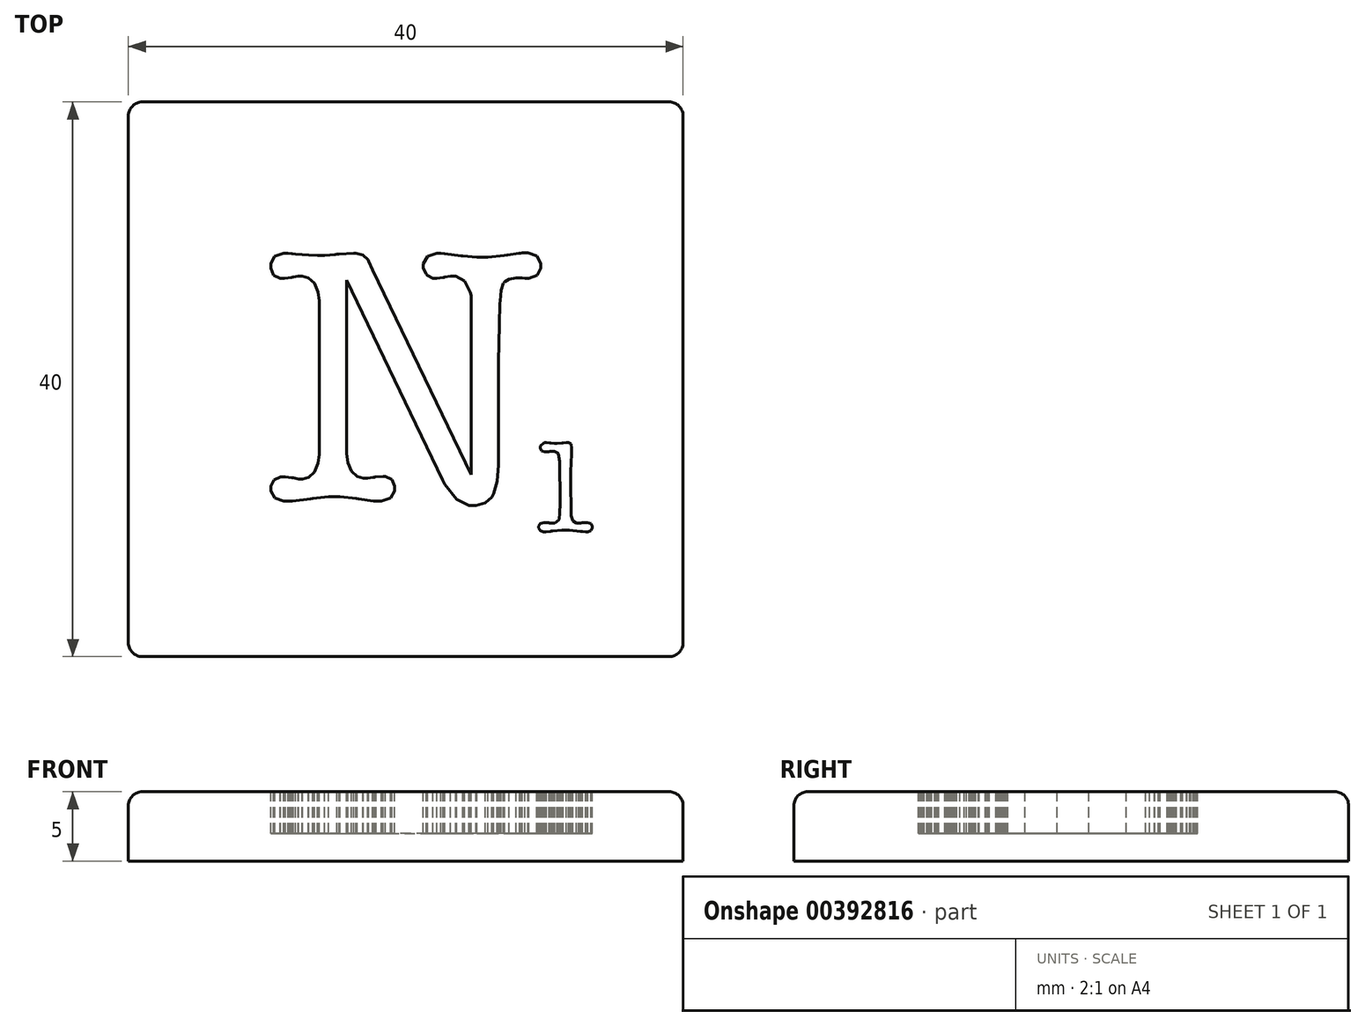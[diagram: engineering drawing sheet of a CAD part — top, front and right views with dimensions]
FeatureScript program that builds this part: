
annotation { "Feature Type Name" : "Feature", "Feature Type Description" : "" }
export const myFeature = defineFeature(function(context is Context, id is Id, definition is map)
    precondition{}
    {
        {
            var Q0;
            Q0=qCreatedBy(makeId("Top.planeOp"),FACE);
            var sketch = newSketch(context, id + "F0", { "sketchPlane" : qUnion([Q0])});
            skLineSegment(sketch, "E0.bottom", {"start": v(20, -20) * mm, "end": v(-20, -20) * mm});
            skLineSegment(sketch, "E0.top", {"start": v(20, 20) * mm, "end": v(-20, 20) * mm});
            skLineSegment(sketch, "E0.left", {"start": v(20, -20) * mm, "end": v(20, 20) * mm});
            skLineSegment(sketch, "E0.right", {"start": v(-20, -20) * mm, "end": v(-20, 20) * mm});
            skPoint(sketch, "E0.middle", {"position": v(0, 0) * mm});
            skSolve(sketch);
        }
        {
            var Q0;
            Q0=makeQuery(id+"F0.imprint","IMPRINT",FACE,{"disambiguationData":[TD([[makeQuery(id+"F0.imprint","IMPRINT",EDGE,{"derivedFrom":sQuery(id+"F0.wireOp",EDGE,"E0.bottom")}),-1.0]])]});
            extrude(context, id + "F1", {"entities" : qUnion([Q0]), "depth" : -5 * mm});
        }
        {
            var Q0;
            Q0=makeQuery(id+"F1.opExtrude","CAP_FACE",FACE,{"disambiguationData":[OSD([sQuery(id+"F0.wireOp",EDGE,"E0.bottom"),sQuery(id+"F0.wireOp",EDGE,"E0.top"),sQuery(id+"F0.wireOp",EDGE,"E0.left"),sQuery(id+"F0.wireOp",EDGE,"E0.right")])],"isStart":true});
            var Q1;
            Q1=makeQuery(id+"F1.opExtrude","SWEPT_EDGE",EDGE,{"disambiguationData":[OSD([sQuery(id+"F0.wireOp",EDGE,"E0.top"),sQuery(id+"F0.wireOp",EDGE,"E0.right")])]});
            var Q2;
            Q2=makeQuery(id+"F1.opExtrude","SWEPT_EDGE",EDGE,{"disambiguationData":[OSD([sQuery(id+"F0.wireOp",EDGE,"E0.top"),sQuery(id+"F0.wireOp",EDGE,"E0.left")])]});
            var Q3;
            Q3=makeQuery(id+"F1.opExtrude","SWEPT_EDGE",EDGE,{"disambiguationData":[OSD([sQuery(id+"F0.wireOp",EDGE,"E0.bottom"),sQuery(id+"F0.wireOp",EDGE,"E0.right")])]});
            var Q4;
            Q4=makeQuery(id+"F1.opExtrude","SWEPT_EDGE",EDGE,{"disambiguationData":[OSD([sQuery(id+"F0.wireOp",EDGE,"E0.bottom"),sQuery(id+"F0.wireOp",EDGE,"E0.left")])]});
            fillet(context, id + "F2", {"entities" : qUnion([Q0, Q1, Q2, Q3, Q4]), "radius" : 1 * mm, "tangentPropagation" : true, "allowEdgeOverflow" : false});
        }
        {
            var Q0;
            Q0=qCreatedBy(makeId("Top.planeOp"),FACE);
            var sketch = newSketch(context, id + "F3", { "sketchPlane" : qUnion([Q0])});
            skLineSegment(sketch, "E1", {"start": v(-2.38, 7.9) * mm, "end": v(4.74, -6.9) * mm});
            skLineSegment(sketch, "E2", {"start": v(4.74, -6.9) * mm, "end": v(4.74, 3.77) * mm});
            skLineSegment(sketch, "E3", {"start": v(4.74, 3.77) * mm, "end": v(4.74, 4.17) * mm});
            skLineSegment(sketch, "E4", {"start": v(4.74, 4.17) * mm, "end": v(4.73, 5.37) * mm});
            skLineSegment(sketch, "E5", {"start": v(4.73, 5.37) * mm, "end": v(4.71, 6.01) * mm});
            skLineSegment(sketch, "E6", {"start": v(4.71, 6.01) * mm, "end": v(4.7, 6.05) * mm});
            skLineSegment(sketch, "E7", {"start": v(4.7, 6.05) * mm, "end": v(4.67, 6.28) * mm});
            skLineSegment(sketch, "E8", {"start": v(4.67, 6.28) * mm, "end": v(4.26, 7.08) * mm});
            skLineSegment(sketch, "E9", {"start": v(4.26, 7.08) * mm, "end": v(3.6, 7.42) * mm});
            skLineSegment(sketch, "E10", {"start": v(3.6, 7.42) * mm, "end": v(3.39, 7.42) * mm});
            skLineSegment(sketch, "E11", {"start": v(3.39, 7.42) * mm, "end": v(3.23, 7.42) * mm});
            skLineSegment(sketch, "E12", {"start": v(3.23, 7.42) * mm, "end": v(2.82, 7.37) * mm});
            skLineSegment(sketch, "E13", {"start": v(2.82, 7.37) * mm, "end": v(2.75, 7.36) * mm});
            skLineSegment(sketch, "E14", {"start": v(2.75, 7.36) * mm, "end": v(2.68, 7.34) * mm});
            skLineSegment(sketch, "E15", {"start": v(2.68, 7.34) * mm, "end": v(2.26, 7.29) * mm});
            skLineSegment(sketch, "E16", {"start": v(2.26, 7.29) * mm, "end": v(2.12, 7.29) * mm});
            skLineSegment(sketch, "E17", {"start": v(2.12, 7.29) * mm, "end": v(1.97, 7.29) * mm});
            skLineSegment(sketch, "E18", {"start": v(1.97, 7.29) * mm, "end": v(1.56, 7.5) * mm});
            skLineSegment(sketch, "E19", {"start": v(1.56, 7.5) * mm, "end": v(1.52, 7.54) * mm});
            skLineSegment(sketch, "E20", {"start": v(1.52, 7.54) * mm, "end": v(1.48, 7.58) * mm});
            skLineSegment(sketch, "E21", {"start": v(1.48, 7.58) * mm, "end": v(1.27, 8) * mm});
            skLineSegment(sketch, "E22", {"start": v(1.27, 8) * mm, "end": v(1.27, 8.14) * mm});
            skLineSegment(sketch, "E23", {"start": v(1.27, 8.14) * mm, "end": v(1.27, 8.32) * mm});
            skLineSegment(sketch, "E24", {"start": v(1.27, 8.32) * mm, "end": v(1.57, 8.85) * mm});
            skLineSegment(sketch, "E25", {"start": v(1.57, 8.85) * mm, "end": v(2.24, 9.09) * mm});
            skLineSegment(sketch, "E26", {"start": v(2.24, 9.09) * mm, "end": v(2.46, 9.09) * mm});
            skLineSegment(sketch, "E27", {"start": v(2.46, 9.09) * mm, "end": v(2.55, 9.09) * mm});
            skLineSegment(sketch, "E28", {"start": v(2.55, 9.09) * mm, "end": v(2.79, 9.07) * mm});
            skLineSegment(sketch, "E29", {"start": v(2.79, 9.07) * mm, "end": v(2.8, 9.06) * mm});
            skLineSegment(sketch, "E30", {"start": v(2.8, 9.06) * mm, "end": v(4, 8.9) * mm});
            skLineSegment(sketch, "E31", {"start": v(4, 8.9) * mm, "end": v(4.13, 8.89) * mm});
            skLineSegment(sketch, "E32", {"start": v(4.13, 8.89) * mm, "end": v(5.14, 8.8) * mm});
            skLineSegment(sketch, "E33", {"start": v(5.14, 8.8) * mm, "end": v(5.48, 8.8) * mm});
            skLineSegment(sketch, "E34", {"start": v(5.48, 8.8) * mm, "end": v(5.93, 8.8) * mm});
            skLineSegment(sketch, "E35", {"start": v(5.93, 8.8) * mm, "end": v(7.11, 8.93) * mm});
            skLineSegment(sketch, "E36", {"start": v(7.11, 8.93) * mm, "end": v(7.3, 8.96) * mm});
            skLineSegment(sketch, "E37", {"start": v(7.3, 8.96) * mm, "end": v(7.37, 8.97) * mm});
            skLineSegment(sketch, "E38", {"start": v(7.37, 8.97) * mm, "end": v(8.14, 9.08) * mm});
            skLineSegment(sketch, "E39", {"start": v(8.14, 9.08) * mm, "end": v(8.23, 9.09) * mm});
            skLineSegment(sketch, "E40", {"start": v(8.23, 9.09) * mm, "end": v(8.27, 9.09) * mm});
            skLineSegment(sketch, "E41", {"start": v(8.27, 9.09) * mm, "end": v(8.4, 9.11) * mm});
            skLineSegment(sketch, "E42", {"start": v(8.4, 9.11) * mm, "end": v(8.41, 9.11) * mm});
            skLineSegment(sketch, "E43", {"start": v(8.41, 9.11) * mm, "end": v(8.6, 9.11) * mm});
            skLineSegment(sketch, "E44", {"start": v(8.6, 9.11) * mm, "end": v(8.81, 9.11) * mm});
            skLineSegment(sketch, "E45", {"start": v(8.81, 9.11) * mm, "end": v(9.45, 8.88) * mm});
            skLineSegment(sketch, "E46", {"start": v(9.45, 8.88) * mm, "end": v(9.74, 8.36) * mm});
            skLineSegment(sketch, "E47", {"start": v(9.74, 8.36) * mm, "end": v(9.74, 8.19) * mm});
            skLineSegment(sketch, "E48", {"start": v(9.74, 8.19) * mm, "end": v(9.74, 8.02) * mm});
            skLineSegment(sketch, "E49", {"start": v(9.74, 8.02) * mm, "end": v(9.47, 7.51) * mm});
            skLineSegment(sketch, "E50", {"start": v(9.47, 7.51) * mm, "end": v(8.88, 7.29) * mm});
            skLineSegment(sketch, "E51", {"start": v(8.88, 7.29) * mm, "end": v(8.68, 7.29) * mm});
            skLineSegment(sketch, "E52", {"start": v(8.68, 7.29) * mm, "end": v(8.6, 7.29) * mm});
            skLineSegment(sketch, "E53", {"start": v(8.6, 7.29) * mm, "end": v(8.4, 7.31) * mm});
            skLineSegment(sketch, "E54", {"start": v(8.4, 7.31) * mm, "end": v(8.39, 7.32) * mm});
            skLineSegment(sketch, "E55", {"start": v(8.39, 7.32) * mm, "end": v(8.12, 7.32) * mm});
            skLineSegment(sketch, "E56", {"start": v(8.12, 7.32) * mm, "end": v(7.96, 7.32) * mm});
            skLineSegment(sketch, "E57", {"start": v(7.96, 7.32) * mm, "end": v(7.47, 7.23) * mm});
            skLineSegment(sketch, "E58", {"start": v(7.47, 7.23) * mm, "end": v(7.13, 7.03) * mm});
            skLineSegment(sketch, "E59", {"start": v(7.13, 7.03) * mm, "end": v(7.1, 6.97) * mm});
            skLineSegment(sketch, "E60", {"start": v(7.1, 6.97) * mm, "end": v(7.05, 6.92) * mm});
            skLineSegment(sketch, "E61", {"start": v(7.05, 6.92) * mm, "end": v(6.9, 6.42) * mm});
            skLineSegment(sketch, "E62", {"start": v(6.9, 6.42) * mm, "end": v(6.8, 5.66) * mm});
            skLineSegment(sketch, "E63", {"start": v(6.8, 5.66) * mm, "end": v(6.8, 5.46) * mm});
            skLineSegment(sketch, "E64", {"start": v(6.8, 5.46) * mm, "end": v(6.75, 3.95) * mm});
            skLineSegment(sketch, "E65", {"start": v(6.75, 3.95) * mm, "end": v(6.7, 1.26) * mm});
            skLineSegment(sketch, "E66", {"start": v(6.7, 1.26) * mm, "end": v(6.7, -5.8) * mm});
            skLineSegment(sketch, "E67", {"start": v(6.7, -5.8) * mm, "end": v(6.7, -6.2) * mm});
            skLineSegment(sketch, "E68", {"start": v(6.7, -6.2) * mm, "end": v(6.6, -7.36) * mm});
            skLineSegment(sketch, "E69", {"start": v(6.6, -7.36) * mm, "end": v(6.35, -8.25) * mm});
            skLineSegment(sketch, "E70", {"start": v(6.35, -8.25) * mm, "end": v(6.28, -8.37) * mm});
            skLineSegment(sketch, "E71", {"start": v(6.28, -8.37) * mm, "end": v(6.21, -8.5) * mm});
            skLineSegment(sketch, "E72", {"start": v(6.21, -8.5) * mm, "end": v(5.72, -8.93) * mm});
            skLineSegment(sketch, "E73", {"start": v(5.72, -8.93) * mm, "end": v(5.08, -9.11) * mm});
            skLineSegment(sketch, "E74", {"start": v(5.08, -9.11) * mm, "end": v(4.87, -9.11) * mm});
            skLineSegment(sketch, "E75", {"start": v(4.87, -9.11) * mm, "end": v(4.57, -9.11) * mm});
            skLineSegment(sketch, "E76", {"start": v(4.57, -9.11) * mm, "end": v(3.67, -8.65) * mm});
            skLineSegment(sketch, "E77", {"start": v(3.67, -8.65) * mm, "end": v(2.82, -7.57) * mm});
            skLineSegment(sketch, "E78", {"start": v(2.82, -7.57) * mm, "end": v(2.67, -7.26) * mm});
            skLineSegment(sketch, "E79", {"start": v(2.67, -7.26) * mm, "end": v(-4.26, 7.16) * mm});
            skLineSegment(sketch, "E80", {"start": v(-4.26, 7.16) * mm, "end": v(-4.26, -5.15) * mm});
            skLineSegment(sketch, "E81", {"start": v(-4.26, -5.15) * mm, "end": v(-4.26, -5.36) * mm});
            skLineSegment(sketch, "E82", {"start": v(-4.26, -5.36) * mm, "end": v(-4.18, -6.01) * mm});
            skLineSegment(sketch, "E83", {"start": v(-4.18, -6.01) * mm, "end": v(-3.92, -6.63) * mm});
            skLineSegment(sketch, "E84", {"start": v(-3.92, -6.63) * mm, "end": v(-3.5, -7) * mm});
            skLineSegment(sketch, "E85", {"start": v(-3.5, -7) * mm, "end": v(-3.06, -7.13) * mm});
            skLineSegment(sketch, "E86", {"start": v(-3.06, -7.13) * mm, "end": v(-2.91, -7.13) * mm});
            skLineSegment(sketch, "E87", {"start": v(-2.91, -7.13) * mm, "end": v(-2.75, -7.13) * mm});
            skLineSegment(sketch, "E88", {"start": v(-2.75, -7.13) * mm, "end": v(-2.35, -7.07) * mm});
            skLineSegment(sketch, "E89", {"start": v(-2.35, -7.07) * mm, "end": v(-2.28, -7.06) * mm});
            skLineSegment(sketch, "E90", {"start": v(-2.28, -7.06) * mm, "end": v(-2.2, -7.05) * mm});
            skLineSegment(sketch, "E91", {"start": v(-2.2, -7.05) * mm, "end": v(-1.64, -7) * mm});
            skLineSegment(sketch, "E92", {"start": v(-1.64, -7) * mm, "end": v(-1.48, -7) * mm});
            skLineSegment(sketch, "E93", {"start": v(-1.48, -7) * mm, "end": v(-1, -7.22) * mm});
            skLineSegment(sketch, "E94", {"start": v(-1, -7.22) * mm, "end": v(-0.8, -7.7) * mm});
            skLineSegment(sketch, "E95", {"start": v(-0.8, -7.7) * mm, "end": v(-0.8, -7.87) * mm});
            skLineSegment(sketch, "E96", {"start": v(-0.8, -7.87) * mm, "end": v(-0.8, -8.04) * mm});
            skLineSegment(sketch, "E97", {"start": v(-0.8, -8.04) * mm, "end": v(-1.1, -8.57) * mm});
            skLineSegment(sketch, "E98", {"start": v(-1.1, -8.57) * mm, "end": v(-1.76, -8.8) * mm});
            skLineSegment(sketch, "E99", {"start": v(-1.76, -8.8) * mm, "end": v(-1.99, -8.8) * mm});
            skLineSegment(sketch, "E100", {"start": v(-1.99, -8.8) * mm, "end": v(-2.14, -8.8) * mm});
            skLineSegment(sketch, "E101", {"start": v(-2.14, -8.8) * mm, "end": v(-2.17, -8.8) * mm});
            skLineSegment(sketch, "E102", {"start": v(-2.17, -8.8) * mm, "end": v(-2.29, -8.77) * mm});
            skLineSegment(sketch, "E103", {"start": v(-2.29, -8.77) * mm, "end": v(-2.33, -8.77) * mm});
            skLineSegment(sketch, "E104", {"start": v(-2.33, -8.77) * mm, "end": v(-3.41, -8.61) * mm});
            skLineSegment(sketch, "E105", {"start": v(-3.41, -8.61) * mm, "end": v(-3.56, -8.6) * mm});
            skLineSegment(sketch, "E106", {"start": v(-3.56, -8.6) * mm, "end": v(-4.72, -8.48) * mm});
            skLineSegment(sketch, "E107", {"start": v(-4.72, -8.48) * mm, "end": v(-5.1, -8.48) * mm});
            skLineSegment(sketch, "E108", {"start": v(-5.1, -8.48) * mm, "end": v(-5.55, -8.48) * mm});
            skLineSegment(sketch, "E109", {"start": v(-5.55, -8.48) * mm, "end": v(-6.7, -8.6) * mm});
            skLineSegment(sketch, "E110", {"start": v(-6.7, -8.6) * mm, "end": v(-6.88, -8.61) * mm});
            skLineSegment(sketch, "E111", {"start": v(-6.88, -8.61) * mm, "end": v(-8.18, -8.77) * mm});
            skLineSegment(sketch, "E112", {"start": v(-8.18, -8.77) * mm, "end": v(-8.22, -8.77) * mm});
            skLineSegment(sketch, "E113", {"start": v(-8.22, -8.77) * mm, "end": v(-8.34, -8.8) * mm});
            skLineSegment(sketch, "E114", {"start": v(-8.34, -8.8) * mm, "end": v(-8.36, -8.8) * mm});
            skLineSegment(sketch, "E115", {"start": v(-8.36, -8.8) * mm, "end": v(-8.57, -8.8) * mm});
            skLineSegment(sketch, "E116", {"start": v(-8.57, -8.8) * mm, "end": v(-8.79, -8.8) * mm});
            skLineSegment(sketch, "E117", {"start": v(-8.79, -8.8) * mm, "end": v(-9.43, -8.57) * mm});
            skLineSegment(sketch, "E118", {"start": v(-9.43, -8.57) * mm, "end": v(-9.71, -8.04) * mm});
            skLineSegment(sketch, "E119", {"start": v(-9.71, -8.04) * mm, "end": v(-9.71, -7.87) * mm});
            skLineSegment(sketch, "E120", {"start": v(-9.71, -7.87) * mm, "end": v(-9.71, -7.72) * mm});
            skLineSegment(sketch, "E121", {"start": v(-9.71, -7.72) * mm, "end": v(-9.5, -7.26) * mm});
            skLineSegment(sketch, "E122", {"start": v(-9.5, -7.26) * mm, "end": v(-9.02, -7.05) * mm});
            skLineSegment(sketch, "E123", {"start": v(-9.02, -7.05) * mm, "end": v(-8.86, -7.05) * mm});
            skLineSegment(sketch, "E124", {"start": v(-8.86, -7.05) * mm, "end": v(-8.69, -7.05) * mm});
            skLineSegment(sketch, "E125", {"start": v(-8.69, -7.05) * mm, "end": v(-8.25, -7.1) * mm});
            skLineSegment(sketch, "E126", {"start": v(-8.25, -7.1) * mm, "end": v(-8.15, -7.1) * mm});
            skLineSegment(sketch, "E127", {"start": v(-8.15, -7.1) * mm, "end": v(-8.1, -7.12) * mm});
            skLineSegment(sketch, "E128", {"start": v(-8.1, -7.12) * mm, "end": v(-7.72, -7.18) * mm});
            skLineSegment(sketch, "E129", {"start": v(-7.72, -7.18) * mm, "end": v(-7.6, -7.18) * mm});
            skLineSegment(sketch, "E130", {"start": v(-7.6, -7.18) * mm, "end": v(-7.45, -7.18) * mm});
            skLineSegment(sketch, "E131", {"start": v(-7.45, -7.18) * mm, "end": v(-7, -7.06) * mm});
            skLineSegment(sketch, "E132", {"start": v(-7, -7.06) * mm, "end": v(-6.58, -6.69) * mm});
            skLineSegment(sketch, "E133", {"start": v(-6.58, -6.69) * mm, "end": v(-6.33, -6.07) * mm});
            skLineSegment(sketch, "E134", {"start": v(-6.33, -6.07) * mm, "end": v(-6.24, -5.42) * mm});
            skLineSegment(sketch, "E135", {"start": v(-6.24, -5.42) * mm, "end": v(-6.24, -5.2) * mm});
            skLineSegment(sketch, "E136", {"start": v(-6.24, -5.2) * mm, "end": v(-6.24, -3.35) * mm});
            skLineSegment(sketch, "E137", {"start": v(-6.24, -3.35) * mm, "end": v(-6.22, -1.02) * mm});
            skLineSegment(sketch, "E138", {"start": v(-6.22, -1.02) * mm, "end": v(-6.22, 1.26) * mm});
            skLineSegment(sketch, "E139", {"start": v(-6.22, 1.26) * mm, "end": v(-6.24, 5.44) * mm});
            skLineSegment(sketch, "E140", {"start": v(-6.24, 5.44) * mm, "end": v(-6.24, 5.66) * mm});
            skLineSegment(sketch, "E141", {"start": v(-6.24, 5.66) * mm, "end": v(-6.33, 6.3) * mm});
            skLineSegment(sketch, "E142", {"start": v(-6.33, 6.3) * mm, "end": v(-6.59, 6.93) * mm});
            skLineSegment(sketch, "E143", {"start": v(-6.59, 6.93) * mm, "end": v(-7.02, 7.3) * mm});
            skLineSegment(sketch, "E144", {"start": v(-7.02, 7.3) * mm, "end": v(-7.47, 7.42) * mm});
            skLineSegment(sketch, "E145", {"start": v(-7.47, 7.42) * mm, "end": v(-7.62, 7.42) * mm});
            skLineSegment(sketch, "E146", {"start": v(-7.62, 7.42) * mm, "end": v(-7.75, 7.42) * mm});
            skLineSegment(sketch, "E147", {"start": v(-7.75, 7.42) * mm, "end": v(-8.1, 7.38) * mm});
            skLineSegment(sketch, "E148", {"start": v(-8.1, 7.38) * mm, "end": v(-8.15, 7.37) * mm});
            skLineSegment(sketch, "E149", {"start": v(-8.15, 7.37) * mm, "end": v(-8.23, 7.36) * mm});
            skLineSegment(sketch, "E150", {"start": v(-8.23, 7.36) * mm, "end": v(-8.73, 7.29) * mm});
            skLineSegment(sketch, "E151", {"start": v(-8.73, 7.29) * mm, "end": v(-8.9, 7.29) * mm});
            skLineSegment(sketch, "E152", {"start": v(-8.9, 7.29) * mm, "end": v(-9.05, 7.29) * mm});
            skLineSegment(sketch, "E153", {"start": v(-9.05, 7.29) * mm, "end": v(-9.53, 7.5) * mm});
            skLineSegment(sketch, "E154", {"start": v(-9.53, 7.5) * mm, "end": v(-9.74, 8) * mm});
            skLineSegment(sketch, "E155", {"start": v(-9.74, 8) * mm, "end": v(-9.74, 8.16) * mm});
            skLineSegment(sketch, "E156", {"start": v(-9.74, 8.16) * mm, "end": v(-9.74, 8.34) * mm});
            skLineSegment(sketch, "E157", {"start": v(-9.74, 8.34) * mm, "end": v(-9.45, 8.86) * mm});
            skLineSegment(sketch, "E158", {"start": v(-9.45, 8.86) * mm, "end": v(-8.81, 9.09) * mm});
            skLineSegment(sketch, "E159", {"start": v(-8.81, 9.09) * mm, "end": v(-8.6, 9.09) * mm});
            skLineSegment(sketch, "E160", {"start": v(-8.6, 9.09) * mm, "end": v(-8.5, 9.09) * mm});
            skLineSegment(sketch, "E161", {"start": v(-8.5, 9.09) * mm, "end": v(-8.22, 9.07) * mm});
            skLineSegment(sketch, "E162", {"start": v(-8.22, 9.07) * mm, "end": v(-8.18, 9.06) * mm});
            skLineSegment(sketch, "E163", {"start": v(-8.18, 9.06) * mm, "end": v(-7.96, 9.04) * mm});
            skLineSegment(sketch, "E164", {"start": v(-7.96, 9.04) * mm, "end": v(-7, 8.96) * mm});
            skLineSegment(sketch, "E165", {"start": v(-7, 8.96) * mm, "end": v(-6.36, 8.93) * mm});
            skLineSegment(sketch, "E166", {"start": v(-6.36, 8.93) * mm, "end": v(-6.14, 8.93) * mm});
            skLineSegment(sketch, "E167", {"start": v(-6.14, 8.93) * mm, "end": v(-5.84, 8.93) * mm});
            skLineSegment(sketch, "E168", {"start": v(-5.84, 8.93) * mm, "end": v(-5.08, 9) * mm});
            skLineSegment(sketch, "E169", {"start": v(-5.08, 9) * mm, "end": v(-4.95, 9) * mm});
            skLineSegment(sketch, "E170", {"start": v(-4.95, 9) * mm, "end": v(-4.82, 9.02) * mm});
            skLineSegment(sketch, "E171", {"start": v(-4.82, 9.02) * mm, "end": v(-3.76, 9.09) * mm});
            skLineSegment(sketch, "E172", {"start": v(-3.76, 9.09) * mm, "end": v(-3.59, 9.09) * mm});
            skLineSegment(sketch, "E173", {"start": v(-3.59, 9.09) * mm, "end": v(-3.08, 8.95) * mm});
            skLineSegment(sketch, "E174", {"start": v(-3.08, 8.95) * mm, "end": v(-2.72, 8.63) * mm});
            skLineSegment(sketch, "E175", {"start": v(-2.72, 8.63) * mm, "end": v(-2.67, 8.53) * mm});
            skLineSegment(sketch, "E176", {"start": v(-2.67, 8.53) * mm, "end": v(-2.38, 7.9) * mm});
            skSolve(sketch);
        }
        {
            var Q0;
            Q0=qCreatedBy(makeId("Top.planeOp"),FACE);
            var sketch = newSketch(context, id + "F4", { "sketchPlane" : qUnion([Q0])});
            skLineSegment(sketch, "E177", {"start": v(11.13, -8.76) * mm, "end": v(11.1, -6) * mm});
            skLineSegment(sketch, "E178", {"start": v(11.1, -6) * mm, "end": v(11.1, -5.92) * mm});
            skLineSegment(sketch, "E179", {"start": v(11.1, -5.92) * mm, "end": v(11.02, -5.38) * mm});
            skLineSegment(sketch, "E180", {"start": v(11.02, -5.38) * mm, "end": v(11, -5.35) * mm});
            skLineSegment(sketch, "E181", {"start": v(11, -5.35) * mm, "end": v(10.99, -5.32) * mm});
            skLineSegment(sketch, "E182", {"start": v(10.99, -5.32) * mm, "end": v(10.73, -5.19) * mm});
            skLineSegment(sketch, "E183", {"start": v(10.73, -5.19) * mm, "end": v(10.64, -5.19) * mm});
            skLineSegment(sketch, "E184", {"start": v(10.64, -5.19) * mm, "end": v(10.57, -5.19) * mm});
            skLineSegment(sketch, "E185", {"start": v(10.57, -5.19) * mm, "end": v(10.4, -5.2) * mm});
            skLineSegment(sketch, "E186", {"start": v(10.4, -5.2) * mm, "end": v(10.37, -5.21) * mm});
            skLineSegment(sketch, "E187", {"start": v(10.37, -5.21) * mm, "end": v(10.34, -5.22) * mm});
            skLineSegment(sketch, "E188", {"start": v(10.34, -5.22) * mm, "end": v(10.15, -5.24) * mm});
            skLineSegment(sketch, "E189", {"start": v(10.15, -5.24) * mm, "end": v(10.1, -5.24) * mm});
            skLineSegment(sketch, "E190", {"start": v(10.1, -5.24) * mm, "end": v(10.02, -5.24) * mm});
            skLineSegment(sketch, "E191", {"start": v(10.02, -5.24) * mm, "end": v(9.81, -5.15) * mm});
            skLineSegment(sketch, "E192", {"start": v(9.81, -5.15) * mm, "end": v(9.72, -4.97) * mm});
            skLineSegment(sketch, "E193", {"start": v(9.72, -4.97) * mm, "end": v(9.72, -4.9) * mm});
            skLineSegment(sketch, "E194", {"start": v(9.72, -4.9) * mm, "end": v(9.72, -4.82) * mm});
            skLineSegment(sketch, "E195", {"start": v(9.72, -4.82) * mm, "end": v(9.98, -4.57) * mm});
            skLineSegment(sketch, "E196", {"start": v(9.98, -4.57) * mm, "end": v(10.07, -4.57) * mm});
            skLineSegment(sketch, "E197", {"start": v(10.07, -4.57) * mm, "end": v(10.16, -4.57) * mm});
            skLineSegment(sketch, "E198", {"start": v(10.16, -4.57) * mm, "end": v(10.39, -4.59) * mm});
            skLineSegment(sketch, "E199", {"start": v(10.39, -4.59) * mm, "end": v(10.43, -4.6) * mm});
            skLineSegment(sketch, "E200", {"start": v(10.43, -4.6) * mm, "end": v(10.47, -4.6) * mm});
            skLineSegment(sketch, "E201", {"start": v(10.47, -4.6) * mm, "end": v(10.72, -4.62) * mm});
            skLineSegment(sketch, "E202", {"start": v(10.72, -4.62) * mm, "end": v(10.8, -4.62) * mm});
            skLineSegment(sketch, "E203", {"start": v(10.8, -4.62) * mm, "end": v(10.93, -4.62) * mm});
            skLineSegment(sketch, "E204", {"start": v(10.93, -4.62) * mm, "end": v(11.28, -4.6) * mm});
            skLineSegment(sketch, "E205", {"start": v(11.28, -4.6) * mm, "end": v(11.3, -4.6) * mm});
            skLineSegment(sketch, "E206", {"start": v(11.3, -4.6) * mm, "end": v(11.36, -4.6) * mm});
            skLineSegment(sketch, "E207", {"start": v(11.36, -4.6) * mm, "end": v(11.6, -4.57) * mm});
            skLineSegment(sketch, "E208", {"start": v(11.6, -4.57) * mm, "end": v(11.67, -4.57) * mm});
            skLineSegment(sketch, "E209", {"start": v(11.67, -4.57) * mm, "end": v(11.74, -4.57) * mm});
            skLineSegment(sketch, "E210", {"start": v(11.74, -4.57) * mm, "end": v(11.92, -4.67) * mm});
            skLineSegment(sketch, "E211", {"start": v(11.92, -4.67) * mm, "end": v(11.93, -4.7) * mm});
            skLineSegment(sketch, "E212", {"start": v(11.93, -4.7) * mm, "end": v(11.93, -4.7) * mm});
            skLineSegment(sketch, "E213", {"start": v(11.93, -4.7) * mm, "end": v(11.97, -4.92) * mm});
            skLineSegment(sketch, "E214", {"start": v(11.97, -4.92) * mm, "end": v(11.97, -4.99) * mm});
            skLineSegment(sketch, "E215", {"start": v(11.97, -4.99) * mm, "end": v(11.97, -5.05) * mm});
            skLineSegment(sketch, "E216", {"start": v(11.97, -5.05) * mm, "end": v(11.96, -5.18) * mm});
            skLineSegment(sketch, "E217", {"start": v(11.96, -5.18) * mm, "end": v(11.96, -5.22) * mm});
            skLineSegment(sketch, "E218", {"start": v(11.96, -5.22) * mm, "end": v(11.95, -5.39) * mm});
            skLineSegment(sketch, "E219", {"start": v(11.95, -5.39) * mm, "end": v(11.91, -6.65) * mm});
            skLineSegment(sketch, "E220", {"start": v(11.91, -6.65) * mm, "end": v(11.91, -7.07) * mm});
            skLineSegment(sketch, "E221", {"start": v(11.91, -7.07) * mm, "end": v(11.91, -8.14) * mm});
            skLineSegment(sketch, "E222", {"start": v(11.91, -8.14) * mm, "end": v(11.92, -8.85) * mm});
            skLineSegment(sketch, "E223", {"start": v(11.92, -8.85) * mm, "end": v(11.92, -8.93) * mm});
            skLineSegment(sketch, "E224", {"start": v(11.92, -8.93) * mm, "end": v(11.92, -9.03) * mm});
            skLineSegment(sketch, "E225", {"start": v(11.92, -9.03) * mm, "end": v(11.94, -9.55) * mm});
            skLineSegment(sketch, "E226", {"start": v(11.94, -9.55) * mm, "end": v(11.94, -9.72) * mm});
            skLineSegment(sketch, "E227", {"start": v(11.94, -9.72) * mm, "end": v(11.94, -9.83) * mm});
            skLineSegment(sketch, "E228", {"start": v(11.94, -9.83) * mm, "end": v(12.05, -10.21) * mm});
            skLineSegment(sketch, "E229", {"start": v(12.05, -10.21) * mm, "end": v(12.3, -10.38) * mm});
            skLineSegment(sketch, "E230", {"start": v(12.3, -10.38) * mm, "end": v(12.38, -10.38) * mm});
            skLineSegment(sketch, "E231", {"start": v(12.38, -10.38) * mm, "end": v(12.46, -10.38) * mm});
            skLineSegment(sketch, "E232", {"start": v(12.46, -10.38) * mm, "end": v(12.66, -10.36) * mm});
            skLineSegment(sketch, "E233", {"start": v(12.66, -10.36) * mm, "end": v(12.7, -10.36) * mm});
            skLineSegment(sketch, "E234", {"start": v(12.7, -10.36) * mm, "end": v(12.73, -10.35) * mm});
            skLineSegment(sketch, "E235", {"start": v(12.73, -10.35) * mm, "end": v(13, -10.33) * mm});
            skLineSegment(sketch, "E236", {"start": v(13, -10.33) * mm, "end": v(13.1, -10.33) * mm});
            skLineSegment(sketch, "E237", {"start": v(13.1, -10.33) * mm, "end": v(13.35, -10.42) * mm});
            skLineSegment(sketch, "E238", {"start": v(13.35, -10.42) * mm, "end": v(13.46, -10.6) * mm});
            skLineSegment(sketch, "E239", {"start": v(13.46, -10.6) * mm, "end": v(13.46, -10.67) * mm});
            skLineSegment(sketch, "E240", {"start": v(13.46, -10.67) * mm, "end": v(13.46, -10.73) * mm});
            skLineSegment(sketch, "E241", {"start": v(13.46, -10.73) * mm, "end": v(13.36, -10.92) * mm});
            skLineSegment(sketch, "E242", {"start": v(13.36, -10.92) * mm, "end": v(13.12, -11) * mm});
            skLineSegment(sketch, "E243", {"start": v(13.12, -11) * mm, "end": v(13.04, -11) * mm});
            skLineSegment(sketch, "E244", {"start": v(13.04, -11) * mm, "end": v(12.97, -11) * mm});
            skLineSegment(sketch, "E245", {"start": v(12.97, -11) * mm, "end": v(12.76, -10.98) * mm});
            skLineSegment(sketch, "E246", {"start": v(12.76, -10.98) * mm, "end": v(12.74, -10.98) * mm});
            skLineSegment(sketch, "E247", {"start": v(12.74, -10.98) * mm, "end": v(12.6, -10.96) * mm});
            skLineSegment(sketch, "E248", {"start": v(12.6, -10.96) * mm, "end": v(11.8, -10.88) * mm});
            skLineSegment(sketch, "E249", {"start": v(11.8, -10.88) * mm, "end": v(11.52, -10.88) * mm});
            skLineSegment(sketch, "E250", {"start": v(11.52, -10.88) * mm, "end": v(11.26, -10.88) * mm});
            skLineSegment(sketch, "E251", {"start": v(11.26, -10.88) * mm, "end": v(10.6, -10.95) * mm});
            skLineSegment(sketch, "E252", {"start": v(10.6, -10.95) * mm, "end": v(10.5, -10.96) * mm});
            skLineSegment(sketch, "E253", {"start": v(10.5, -10.96) * mm, "end": v(10.43, -10.97) * mm});
            skLineSegment(sketch, "E254", {"start": v(10.43, -10.97) * mm, "end": v(10.11, -11) * mm});
            skLineSegment(sketch, "E255", {"start": v(10.11, -11) * mm, "end": v(10, -11) * mm});
            skLineSegment(sketch, "E256", {"start": v(10, -11) * mm, "end": v(9.93, -11) * mm});
            skLineSegment(sketch, "E257", {"start": v(9.93, -11) * mm, "end": v(9.7, -10.92) * mm});
            skLineSegment(sketch, "E258", {"start": v(9.7, -10.92) * mm, "end": v(9.6, -10.73) * mm});
            skLineSegment(sketch, "E259", {"start": v(9.6, -10.73) * mm, "end": v(9.6, -10.67) * mm});
            skLineSegment(sketch, "E260", {"start": v(9.6, -10.67) * mm, "end": v(9.6, -10.6) * mm});
            skLineSegment(sketch, "E261", {"start": v(9.6, -10.6) * mm, "end": v(9.71, -10.42) * mm});
            skLineSegment(sketch, "E262", {"start": v(9.71, -10.42) * mm, "end": v(9.97, -10.33) * mm});
            skLineSegment(sketch, "E263", {"start": v(9.97, -10.33) * mm, "end": v(10.06, -10.33) * mm});
            skLineSegment(sketch, "E264", {"start": v(10.06, -10.33) * mm, "end": v(10.14, -10.33) * mm});
            skLineSegment(sketch, "E265", {"start": v(10.14, -10.33) * mm, "end": v(10.33, -10.36) * mm});
            skLineSegment(sketch, "E266", {"start": v(10.33, -10.36) * mm, "end": v(10.36, -10.36) * mm});
            skLineSegment(sketch, "E267", {"start": v(10.36, -10.36) * mm, "end": v(10.4, -10.36) * mm});
            skLineSegment(sketch, "E268", {"start": v(10.4, -10.36) * mm, "end": v(10.58, -10.38) * mm});
            skLineSegment(sketch, "E269", {"start": v(10.58, -10.38) * mm, "end": v(10.64, -10.38) * mm});
            skLineSegment(sketch, "E270", {"start": v(10.64, -10.38) * mm, "end": v(10.75, -10.38) * mm});
            skLineSegment(sketch, "E271", {"start": v(10.75, -10.38) * mm, "end": v(11.04, -10.16) * mm});
            skLineSegment(sketch, "E272", {"start": v(11.04, -10.16) * mm, "end": v(11.05, -10.12) * mm});
            skLineSegment(sketch, "E273", {"start": v(11.05, -10.12) * mm, "end": v(11.07, -10.07) * mm});
            skLineSegment(sketch, "E274", {"start": v(11.07, -10.07) * mm, "end": v(11.1, -9.65) * mm});
            skLineSegment(sketch, "E275", {"start": v(11.1, -9.65) * mm, "end": v(11.13, -8.98) * mm});
            skLineSegment(sketch, "E276", {"start": v(11.13, -8.98) * mm, "end": v(11.13, -8.76) * mm});
            skSolve(sketch);
        }
        {
            var Q0;
            Q0 = qSketchRegion(id + "F3", true);
            var Q1;
            Q1 = qSketchRegion(id + "F4", true);
            extrude(context, id + "F5", {"entities" : qUnion([Q0, Q1]), "depth" : -3 * mm});
        }
    });
